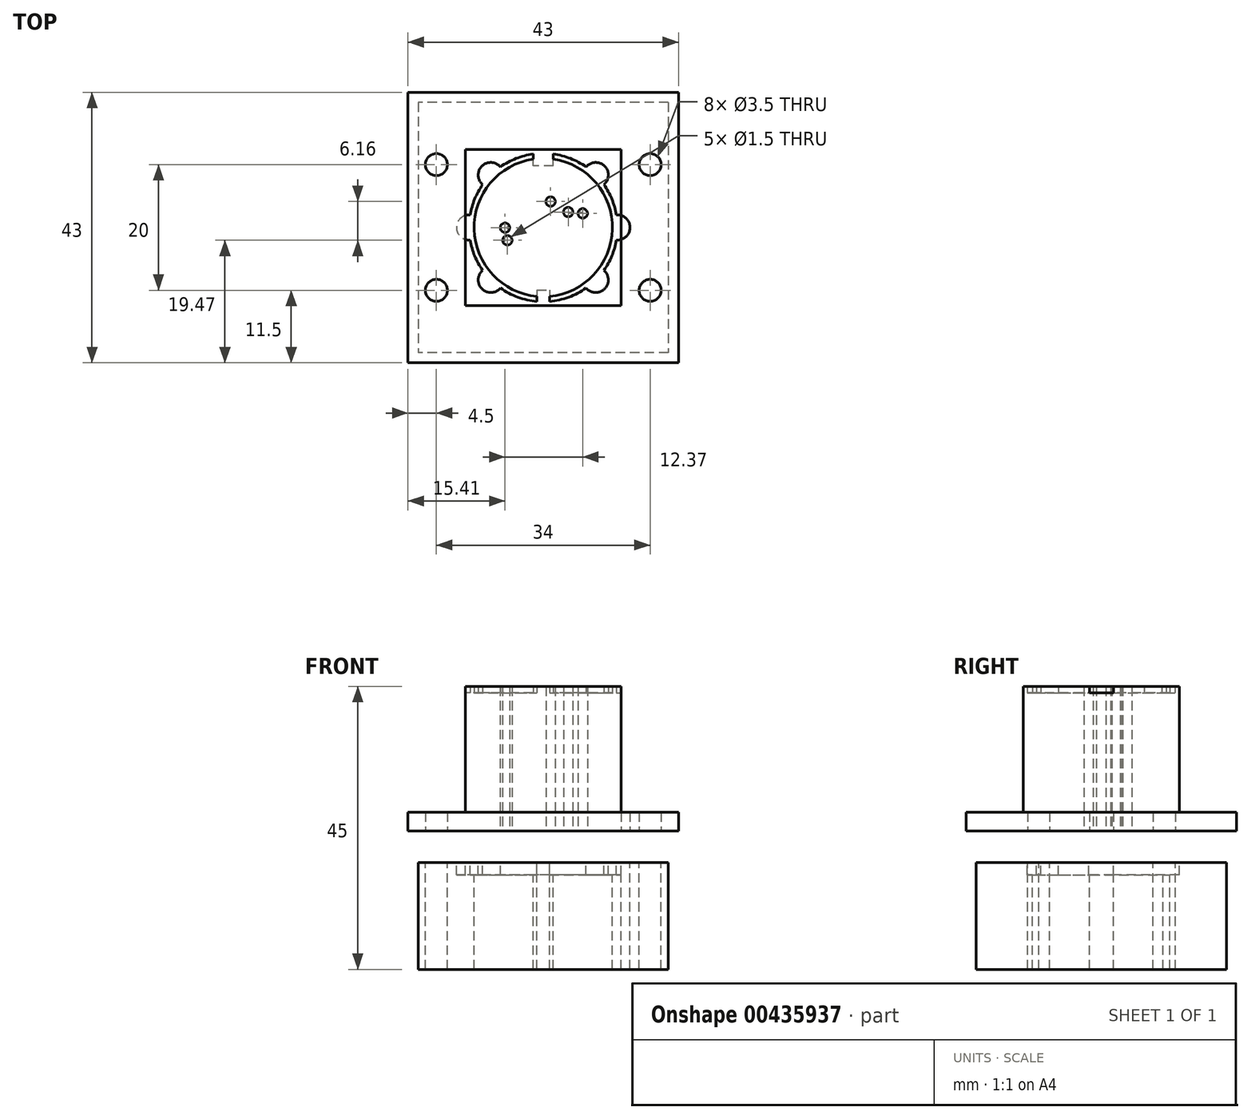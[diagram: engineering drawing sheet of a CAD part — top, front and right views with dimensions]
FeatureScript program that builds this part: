
annotation { "Feature Type Name" : "Feature", "Feature Type Description" : "" }
export const myFeature = defineFeature(function(context is Context, id is Id, definition is map)
    precondition{}
    {
        {
            var Q0;
            Q0=qCreatedBy(makeId("Top.planeOp"),FACE);
            var sketch = newSketch(context, id + "F0", { "sketchPlane" : qUnion([Q0])});
            skPoint(sketch, "E0", {"position": v(0, 0) * mm});
            skPoint(sketch, "E1", {"position": v(-6.1, -0.04) * mm});
            skPoint(sketch, "E2", {"position": v(-5.71, -2.03) * mm});
            skPoint(sketch, "E3", {"position": v(1.16, 4.13) * mm});
            skPoint(sketch, "E4", {"position": v(3.97, 2.45) * mm});
            skPoint(sketch, "E5", {"position": v(6.28, 2.24) * mm});
            skArc(sketch, "E6", {"start": v(-1.6, 11.7) * mm, "mid": v(-4.33, 10.98) * mm, "end": v(-6.81, 9.63) * mm});
            skPoint(sketch, "E7", {"position": v(0, 11.8) * mm});
            skPoint(sketch, "E8", {"position": v(0, -11.8) * mm});
            skPoint(sketch, "E9", {"position": v(11.8, 0) * mm});
            skPoint(sketch, "E10", {"position": v(-11.8, 0) * mm});
            skPoint(sketch, "E11", {"position": v(-8.34, 8.34) * mm});
            skPoint(sketch, "E12", {"position": v(8.34, 8.34) * mm});
            skLineSegment(sketch, "E13", {"start": v(-11.8, 0) * mm, "end": v(11.8, 0) * mm, "construction": true});
            skLineSegment(sketch, "E14", {"start": v(0, 11.8) * mm, "end": v(0, -11.8) * mm, "construction": true});
            skLineSegment(sketch, "E15", {"start": v(-8.34, 8.34) * mm, "end": v(0, 0) * mm, "construction": true});
            skLineSegment(sketch, "E16", {"start": v(8.34, 8.34) * mm, "end": v(0, 0) * mm, "construction": true});
            skLineSegment(sketch, "E17", {"start": v(8.34, -8.34) * mm, "end": v(0, 0) * mm, "construction": true});
            skLineSegment(sketch, "E18", {"start": v(-8.34, -8.34) * mm, "end": v(0, 0) * mm, "construction": true});
            skPoint(sketch, "E19", {"position": v(-8.34, -8.34) * mm});
            skPoint(sketch, "E20", {"position": v(8.34, -8.34) * mm});
            skLineSegment(sketch, "E21.bottom", {"start": v(1.6, 9.8) * mm, "end": v(-1.6, 9.8) * mm});
            skLineSegment(sketch, "E21.left", {"start": v(1.6, 9.8) * mm, "end": v(1.6, 11.7) * mm});
            skLineSegment(sketch, "E21.right", {"start": v(-1.6, 9.8) * mm, "end": v(-1.6, 11.7) * mm});
            skPoint(sketch, "E22", {"position": v(-1.6, 11.7) * mm});
            skPoint(sketch, "E23", {"position": v(1.6, 11.7) * mm});
            skLineSegment(sketch, "E24.bottom", {"start": v(-1, -9.97) * mm, "end": v(1, -9.97) * mm});
            skLineSegment(sketch, "E24.left", {"start": v(-1, -9.97) * mm, "end": v(-1, -11.76) * mm});
            skLineSegment(sketch, "E24.right", {"start": v(1, -9.97) * mm, "end": v(1, -11.76) * mm});
            skPoint(sketch, "E25", {"position": v(-1, -11.76) * mm});
            skPoint(sketch, "E26", {"position": v(1, -11.76) * mm});
            skArc(sketch, "E27.trimOffspring", {"start": v(1, -11.76) * mm, "mid": v(4.05, -11.08) * mm, "end": v(6.81, -9.63) * mm});
            skArc(sketch, "E28", {"start": v(-6.81, 9.63) * mm, "mid": v(-9.76, 9.76) * mm, "end": v(-9.63, 6.81) * mm});
            skArc(sketch, "E29", {"start": v(6.81, 9.63) * mm, "mid": v(9.76, 9.76) * mm, "end": v(9.63, 6.81) * mm});
            skArc(sketch, "E30", {"start": v(9.63, -6.81) * mm, "mid": v(9.76, -9.76) * mm, "end": v(6.81, -9.63) * mm});
            skArc(sketch, "E31", {"start": v(-9.63, -6.81) * mm, "mid": v(-9.76, -9.76) * mm, "end": v(-6.81, -9.63) * mm});
            skArc(sketch, "E32", {"start": v(-1.6, 10.88) * mm, "mid": v(-11, -0.3) * mm, "end": v(-1, -10.95) * mm});
            skCircle(sketch, "E33", {"center": v(6.28, 2.24) * mm, "radius": 0.75 * mm});
            skCircle(sketch, "E34", {"center": v(3.97, 2.45) * mm, "radius": 0.75 * mm});
            skCircle(sketch, "E35", {"center": v(1.16, 4.13) * mm, "radius": 0.75 * mm});
            skCircle(sketch, "E36", {"center": v(-6.1, -0.04) * mm, "radius": 0.75 * mm});
            skCircle(sketch, "E37", {"center": v(-5.71, -2.03) * mm, "radius": 0.75 * mm});
            skArc(sketch, "E38.trimOffspring", {"start": v(-9.63, 6.81) * mm, "mid": v(-10.9, 4.52) * mm, "end": v(-11.63, 2) * mm});
            skArc(sketch, "E39.trimOffspring", {"start": v(6.81, 9.63) * mm, "mid": v(4.33, 10.98) * mm, "end": v(1.6, 11.7) * mm});
            skArc(sketch, "E40.trimOffspring", {"start": v(-6.81, -9.63) * mm, "mid": v(-4.05, -11.08) * mm, "end": v(-1, -11.76) * mm});
            skArc(sketch, "E41.trimOffspring", {"start": v(9.63, -6.81) * mm, "mid": v(10.9, -4.52) * mm, "end": v(11.63, -2) * mm});
            skArc(sketch, "E42.trimOffspring", {"start": v(1, -10.95) * mm, "mid": v(11, -0.3) * mm, "end": v(1.6, 10.88) * mm});
            skPoint(sketch, "E43", {"position": v(1, -10.95) * mm});
            skArc(sketch, "E44", {"start": v(11.63, 2) * mm, "mid": v(13.8, 0) * mm, "end": v(11.63, -2) * mm});
            skArc(sketch, "E45", {"start": v(-11.63, 2) * mm, "mid": v(-13.8, 0) * mm, "end": v(-11.63, -2) * mm});
            skArc(sketch, "E46.trimOffspring", {"start": v(-11.63, -2) * mm, "mid": v(-10.9, -4.52) * mm, "end": v(-9.63, -6.81) * mm});
            skArc(sketch, "E47.trimOffspring", {"start": v(11.63, 2) * mm, "mid": v(10.9, 4.52) * mm, "end": v(9.63, 6.81) * mm});
            skLineSegment(sketch, "E48.bottom", {"start": v(20, 20) * mm, "end": v(-20, 20) * mm, "construction": true});
            skLineSegment(sketch, "E48.top", {"start": v(20, -20) * mm, "end": v(-20, -20) * mm, "construction": true});
            skLineSegment(sketch, "E48.left", {"start": v(20, 20) * mm, "end": v(20, -20) * mm, "construction": true});
            skLineSegment(sketch, "E48.right", {"start": v(-20, 20) * mm, "end": v(-20, -20) * mm, "construction": true});
            skLineSegment(sketch, "E49.bottom", {"start": v(12.5, 12.5) * mm, "end": v(-12.5, 12.5) * mm, "construction": true});
            skLineSegment(sketch, "E49.top", {"start": v(12.5, -12.5) * mm, "end": v(-12.5, -12.5) * mm, "construction": true});
            skLineSegment(sketch, "E49.left", {"start": v(12.5, 12.5) * mm, "end": v(12.5, -12.5) * mm, "construction": true});
            skLineSegment(sketch, "E49.right", {"start": v(-12.5, 12.5) * mm, "end": v(-12.5, -12.5) * mm, "construction": true});
            skPoint(sketch, "E50", {"position": v(-17, 10) * mm});
            skPoint(sketch, "E51", {"position": v(-17, -10) * mm});
            skPoint(sketch, "E52", {"position": v(17, 10) * mm});
            skPoint(sketch, "E53", {"position": v(17, -10) * mm});
            skCircle(sketch, "E54", {"center": v(-17, 10) * mm, "radius": 1.75 * mm});
            skCircle(sketch, "E55", {"center": v(-17, -10) * mm, "radius": 1.75 * mm});
            skCircle(sketch, "E56", {"center": v(17, -10) * mm, "radius": 1.75 * mm});
            skCircle(sketch, "E57", {"center": v(17, 10) * mm, "radius": 1.75 * mm});
            skLineSegment(sketch, "E58.bottom", {"start": v(21.5, -21.5) * mm, "end": v(-21.5, -21.5) * mm});
            skLineSegment(sketch, "E58.top", {"start": v(21.5, 21.5) * mm, "end": v(-21.5, 21.5) * mm});
            skLineSegment(sketch, "E58.left", {"start": v(21.5, -21.5) * mm, "end": v(21.5, 21.5) * mm});
            skLineSegment(sketch, "E58.right", {"start": v(-21.5, -21.5) * mm, "end": v(-21.5, 21.5) * mm});
            skLineSegment(sketch, "E59.0", {"start": v(12.4, 12.4) * mm, "end": v(-12.4, 12.4) * mm});
            skLineSegment(sketch, "E59.1", {"start": v(12.4, 12.4) * mm, "end": v(12.4, -12.4) * mm});
            skLineSegment(sketch, "E59.2", {"start": v(12.4, -12.4) * mm, "end": v(-12.4, -12.4) * mm});
            skLineSegment(sketch, "E59.3", {"start": v(-12.4, 12.4) * mm, "end": v(-12.4, -12.4) * mm});
            skLineSegment(sketch, "E60.0", {"start": v(19.9, 19.9) * mm, "end": v(-19.9, 19.9) * mm});
            skLineSegment(sketch, "E60.1", {"start": v(19.9, 19.9) * mm, "end": v(19.9, -19.9) * mm});
            skLineSegment(sketch, "E60.2", {"start": v(19.9, -19.9) * mm, "end": v(-19.9, -19.9) * mm});
            skLineSegment(sketch, "E60.3", {"start": v(-19.9, 19.9) * mm, "end": v(-19.9, -19.9) * mm});
            skSolve(sketch);
        }
        {
            var Q0;
            {var subQ9=sQuery(id+"F0.wireOp",EDGE,"E6");Q0=makeQuery(id+"F0.imprint","IMPRINT",FACE,{"disambiguationData":[TD([[makeQuery(id+"F0.imprint","IMPRINT",EDGE,{"derivedFrom":subQ9}),-1.0]])]});}
            var Q1;
            {var subQ5=sQuery(id+"F0.wireOp",EDGE,"E21.bottom");Q1=makeQuery(id+"F0.imprint","IMPRINT",FACE,{"disambiguationData":[TD([[makeQuery(id+"F0.imprint","IMPRINT",EDGE,{"derivedFrom":subQ5}),1.0]])]});}
            var Q2;
            {var subQ4=sQuery(id+"F0.wireOp",EDGE,"E6");Q2=makeQuery(id+"F0.imprint","IMPRINT",FACE,{"disambiguationData":[TD([[makeQuery(id+"F0.imprint","IMPRINT",EDGE,{"derivedFrom":subQ4}),1.0]])]});}
            var Q3;
            {var subQ0=sQuery(id+"F0.wireOp",EDGE,"E27.trimOffspring");Q3=makeQuery(id+"F0.imprint","IMPRINT",FACE,{"disambiguationData":[TD([[makeQuery(id+"F0.imprint","IMPRINT",EDGE,{"derivedFrom":subQ0}),1.0]])]});}
            var Q4;
            {var subQ7=sQuery(id+"F0.wireOp",EDGE,"E24.bottom");Q4=makeQuery(id+"F0.imprint","IMPRINT",FACE,{"disambiguationData":[TD([[makeQuery(id+"F0.imprint","IMPRINT",EDGE,{"derivedFrom":subQ7}),-1.0]])]});}
            var Q5;
            Q5=makeQuery(id+"F0.imprint","IMPRINT",FACE,{"disambiguationData":[TD([[makeQuery(id+"F0.imprint","IMPRINT",EDGE,{"derivedFrom":sQuery(id+"F0.wireOp",EDGE,"E54")}),-1.0]])]});
            var Q6;
            {var subQ0=sQuery(id+"F0.wireOp",EDGE,"E59.3");var subQ1=sQuery(id+"F0.wireOp",EDGE,"E45");var subQ2=makeQuery(id+"F0.imprint","INTERSECT",VERTEX,{"disambiguationData":[OD(0.0)],"derivedFrom":[subQ1,subQ0]});Q6=makeQuery(id+"F0.imprint","IMPRINT",FACE,{"disambiguationData":[TD([[makeQuery(id+"F0.imprint","IMPRINT",EDGE,{"disambiguationData":[TD([[subQ2,-1.0]])],"derivedFrom":subQ1}),1.0]])]});}
            var Q7;
            {var subQ0=sQuery(id+"F0.wireOp",EDGE,"E59.1");var subQ1=sQuery(id+"F0.wireOp",EDGE,"E44");var subQ2=makeQuery(id+"F0.imprint","INTERSECT",VERTEX,{"disambiguationData":[OD(0.0)],"derivedFrom":[subQ1,subQ0]});Q7=makeQuery(id+"F0.imprint","IMPRINT",FACE,{"disambiguationData":[TD([[makeQuery(id+"F0.imprint","IMPRINT",EDGE,{"disambiguationData":[TD([[subQ2,-1.0]])],"derivedFrom":subQ1}),-1.0]])]});}
            var Q8;
            Q8=makeQuery(id+"F0.imprint","IMPRINT",FACE,{"disambiguationData":[TD([[makeQuery(id+"F0.imprint","IMPRINT",EDGE,{"derivedFrom":sQuery(id+"F0.wireOp",EDGE,"E58.bottom")}),-1.0]])]});
            extrude(context, id + "F1", {"entities" : qUnion([Q0, Q1, Q2, Q3, Q4, Q5, Q6, Q7, Q8]), "depth" : 8 * mm, "hasSecondDirection" : true, "secondDirectionOppositeDirection" : false, "secondDirectionDepth" : 5 * mm});
        }
        {
            var Q0;
            {var subQ1=sQuery(id+"F0.wireOp",EDGE,"E6");Q0=makeQuery(id+"F0.imprint","IMPRINT",FACE,{"disambiguationData":[TD([[makeQuery(id+"F0.imprint","IMPRINT",EDGE,{"derivedFrom":subQ1}),-1.0]])]});}
            var Q1;
            {var subQ5=sQuery(id+"F0.wireOp",EDGE,"E21.bottom");Q1=makeQuery(id+"F0.imprint","IMPRINT",FACE,{"disambiguationData":[TD([[makeQuery(id+"F0.imprint","IMPRINT",EDGE,{"derivedFrom":subQ5}),1.0]])]});}
            var Q2;
            {var subQ6=sQuery(id+"F0.wireOp",EDGE,"E6");Q2=makeQuery(id+"F0.imprint","IMPRINT",FACE,{"disambiguationData":[TD([[makeQuery(id+"F0.imprint","IMPRINT",EDGE,{"derivedFrom":subQ6}),1.0]])]});}
            var Q3;
            {var subQ7=sQuery(id+"F0.wireOp",EDGE,"E24.bottom");Q3=makeQuery(id+"F0.imprint","IMPRINT",FACE,{"disambiguationData":[TD([[makeQuery(id+"F0.imprint","IMPRINT",EDGE,{"derivedFrom":subQ7}),-1.0]])]});}
            var Q4;
            {var subQ9=sQuery(id+"F0.wireOp",EDGE,"E27.trimOffspring");Q4=makeQuery(id+"F0.imprint","IMPRINT",FACE,{"disambiguationData":[TD([[makeQuery(id+"F0.imprint","IMPRINT",EDGE,{"derivedFrom":subQ9}),1.0]])]});}
            extrude(context, id + "F2", {"entities" : qUnion([Q0, Q1, Q2, Q3, Q4]), "operationType" : NewBodyOperationType.ADD, "depth" : 28 * mm, "hasSecondDirection" : true, "secondDirectionOppositeDirection" : false, "secondDirectionDepth" : 8 * mm});
        }
        {
            var Q0;
            {var subQ6=sQuery(id+"F0.wireOp",EDGE,"E6");Q0=makeQuery(id+"F0.imprint","IMPRINT",FACE,{"disambiguationData":[TD([[makeQuery(id+"F0.imprint","IMPRINT",EDGE,{"derivedFrom":subQ6}),1.0]])]});}
            var Q1;
            {var subQ9=sQuery(id+"F0.wireOp",EDGE,"E27.trimOffspring");Q1=makeQuery(id+"F0.imprint","IMPRINT",FACE,{"disambiguationData":[TD([[makeQuery(id+"F0.imprint","IMPRINT",EDGE,{"derivedFrom":subQ9}),1.0]])]});}
            extrude(context, id + "F3", {"entities" : qUnion([Q0, Q1]), "operationType" : NewBodyOperationType.REMOVE, "depth" : 28 * mm, "hasSecondDirection" : true, "secondDirectionOppositeDirection" : false, "secondDirectionDepth" : 27 * mm});
        }
        {
            var Q0;
            Q0=makeQuery(id+"F0.imprint","IMPRINT",FACE,{"disambiguationData":[TD([[makeQuery(id+"F0.imprint","IMPRINT",EDGE,{"derivedFrom":sQuery(id+"F0.wireOp",EDGE,"E54")}),-1.0]])]});
            var Q1;
            {var subQ1=sQuery(id+"F0.wireOp",EDGE,"E6");Q1=makeQuery(id+"F0.imprint","IMPRINT",FACE,{"disambiguationData":[TD([[makeQuery(id+"F0.imprint","IMPRINT",EDGE,{"derivedFrom":subQ1}),-1.0]])]});}
            var Q2;
            {var subQ7=sQuery(id+"F0.wireOp",EDGE,"E24.bottom");Q2=makeQuery(id+"F0.imprint","IMPRINT",FACE,{"disambiguationData":[TD([[makeQuery(id+"F0.imprint","IMPRINT",EDGE,{"derivedFrom":subQ7}),-1.0]])]});}
            var Q3;
            {var subQ5=sQuery(id+"F0.wireOp",EDGE,"E21.bottom");Q3=makeQuery(id+"F0.imprint","IMPRINT",FACE,{"disambiguationData":[TD([[makeQuery(id+"F0.imprint","IMPRINT",EDGE,{"derivedFrom":subQ5}),1.0]])]});}
            var Q4;
            {var subQ6=sQuery(id+"F0.wireOp",EDGE,"E6");Q4=makeQuery(id+"F0.imprint","IMPRINT",FACE,{"disambiguationData":[TD([[makeQuery(id+"F0.imprint","IMPRINT",EDGE,{"derivedFrom":subQ6}),1.0]])]});}
            var Q5;
            {var subQ9=sQuery(id+"F0.wireOp",EDGE,"E27.trimOffspring");Q5=makeQuery(id+"F0.imprint","IMPRINT",FACE,{"disambiguationData":[TD([[makeQuery(id+"F0.imprint","IMPRINT",EDGE,{"derivedFrom":subQ9}),1.0]])]});}
            var Q6;
            {var subQ0=sQuery(id+"F0.wireOp",EDGE,"E59.3");var subQ1=sQuery(id+"F0.wireOp",EDGE,"E45");var subQ2=makeQuery(id+"F0.imprint","INTERSECT",VERTEX,{"disambiguationData":[OD(0.0)],"derivedFrom":[subQ1,subQ0]});Q6=makeQuery(id+"F0.imprint","IMPRINT",FACE,{"disambiguationData":[TD([[makeQuery(id+"F0.imprint","IMPRINT",EDGE,{"disambiguationData":[TD([[subQ2,-1.0]])],"derivedFrom":subQ1}),1.0]])]});}
            var Q7;
            {var subQ0=sQuery(id+"F0.wireOp",EDGE,"E59.1");var subQ1=sQuery(id+"F0.wireOp",EDGE,"E44");var subQ2=makeQuery(id+"F0.imprint","INTERSECT",VERTEX,{"disambiguationData":[OD(0.0)],"derivedFrom":[subQ1,subQ0]});Q7=makeQuery(id+"F0.imprint","IMPRINT",FACE,{"disambiguationData":[TD([[makeQuery(id+"F0.imprint","IMPRINT",EDGE,{"disambiguationData":[TD([[subQ2,-1.0]])],"derivedFrom":subQ1}),-1.0]])]});}
            var Q8;
            Q8=makeQuery(id+"F0.imprint","IMPRINT",FACE,{"disambiguationData":[TD([[makeQuery(id+"F0.imprint","IMPRINT",EDGE,{"derivedFrom":sQuery(id+"F0.wireOp",EDGE,"E33")}),1.0]])]});
            var Q9;
            Q9=makeQuery(id+"F0.imprint","IMPRINT",FACE,{"disambiguationData":[TD([[makeQuery(id+"F0.imprint","IMPRINT",EDGE,{"derivedFrom":sQuery(id+"F0.wireOp",EDGE,"E34")}),1.0]])]});
            var Q10;
            Q10=makeQuery(id+"F0.imprint","IMPRINT",FACE,{"disambiguationData":[TD([[makeQuery(id+"F0.imprint","IMPRINT",EDGE,{"derivedFrom":sQuery(id+"F0.wireOp",EDGE,"E35")}),1.0]])]});
            var Q11;
            Q11=makeQuery(id+"F0.imprint","IMPRINT",FACE,{"disambiguationData":[TD([[makeQuery(id+"F0.imprint","IMPRINT",EDGE,{"derivedFrom":sQuery(id+"F0.wireOp",EDGE,"E36")}),1.0]])]});
            var Q12;
            Q12=makeQuery(id+"F0.imprint","IMPRINT",FACE,{"disambiguationData":[TD([[makeQuery(id+"F0.imprint","IMPRINT",EDGE,{"derivedFrom":sQuery(id+"F0.wireOp",EDGE,"E37")}),1.0]])]});
            extrude(context, id + "F4", {"entities" : qUnion([Q0, Q1, Q2, Q3, Q4, Q5, Q6, Q7, Q8, Q9, Q10, Q11, Q12]), "oppositeDirection" : true, "depth" : 17 * mm});
        }
        {
            var Q0;
            {var subQ6=sQuery(id+"F0.wireOp",EDGE,"E6");Q0=makeQuery(id+"F0.imprint","IMPRINT",FACE,{"disambiguationData":[TD([[makeQuery(id+"F0.imprint","IMPRINT",EDGE,{"derivedFrom":subQ6}),1.0]])]});}
            var Q1;
            {var subQ5=sQuery(id+"F0.wireOp",EDGE,"E21.bottom");Q1=makeQuery(id+"F0.imprint","IMPRINT",FACE,{"disambiguationData":[TD([[makeQuery(id+"F0.imprint","IMPRINT",EDGE,{"derivedFrom":subQ5}),1.0]])]});}
            var Q2;
            {var subQ0=sQuery(id+"F0.wireOp",EDGE,"E59.3");var subQ1=sQuery(id+"F0.wireOp",EDGE,"E45");var subQ2=makeQuery(id+"F0.imprint","INTERSECT",VERTEX,{"disambiguationData":[OD(0.0)],"derivedFrom":[subQ1,subQ0]});Q2=makeQuery(id+"F0.imprint","IMPRINT",FACE,{"disambiguationData":[TD([[makeQuery(id+"F0.imprint","IMPRINT",EDGE,{"disambiguationData":[TD([[subQ2,-1.0]])],"derivedFrom":subQ1}),1.0]])]});}
            var Q3;
            {var subQ9=sQuery(id+"F0.wireOp",EDGE,"E27.trimOffspring");Q3=makeQuery(id+"F0.imprint","IMPRINT",FACE,{"disambiguationData":[TD([[makeQuery(id+"F0.imprint","IMPRINT",EDGE,{"derivedFrom":subQ9}),1.0]])]});}
            var Q4;
            {var subQ0=sQuery(id+"F0.wireOp",EDGE,"E59.1");var subQ1=sQuery(id+"F0.wireOp",EDGE,"E44");var subQ2=makeQuery(id+"F0.imprint","INTERSECT",VERTEX,{"disambiguationData":[OD(0.0)],"derivedFrom":[subQ1,subQ0]});Q4=makeQuery(id+"F0.imprint","IMPRINT",FACE,{"disambiguationData":[TD([[makeQuery(id+"F0.imprint","IMPRINT",EDGE,{"disambiguationData":[TD([[subQ2,-1.0]])],"derivedFrom":subQ1}),-1.0]])]});}
            var Q5;
            Q5=makeQuery(id+"F0.imprint","IMPRINT",FACE,{"disambiguationData":[TD([[makeQuery(id+"F0.imprint","IMPRINT",EDGE,{"derivedFrom":sQuery(id+"F0.wireOp",EDGE,"E37")}),1.0]])]});
            var Q6;
            Q6=makeQuery(id+"F0.imprint","IMPRINT",FACE,{"disambiguationData":[TD([[makeQuery(id+"F0.imprint","IMPRINT",EDGE,{"derivedFrom":sQuery(id+"F0.wireOp",EDGE,"E36")}),1.0]])]});
            var Q7;
            Q7=makeQuery(id+"F0.imprint","IMPRINT",FACE,{"disambiguationData":[TD([[makeQuery(id+"F0.imprint","IMPRINT",EDGE,{"derivedFrom":sQuery(id+"F0.wireOp",EDGE,"E35")}),1.0]])]});
            var Q8;
            Q8=makeQuery(id+"F0.imprint","IMPRINT",FACE,{"disambiguationData":[TD([[makeQuery(id+"F0.imprint","IMPRINT",EDGE,{"derivedFrom":sQuery(id+"F0.wireOp",EDGE,"E34")}),1.0]])]});
            var Q9;
            Q9=makeQuery(id+"F0.imprint","IMPRINT",FACE,{"disambiguationData":[TD([[makeQuery(id+"F0.imprint","IMPRINT",EDGE,{"derivedFrom":sQuery(id+"F0.wireOp",EDGE,"E33")}),1.0]])]});
            extrude(context, id + "F5", {"entities" : qUnion([Q0, Q1, Q2, Q3, Q4, Q5, Q6, Q7, Q8, Q9]), "operationType" : NewBodyOperationType.REMOVE, "oppositeDirection" : true, "depth" : 2 * mm});
        }
        {
            var Q0;
            {var subQ5=sQuery(id+"F0.wireOp",EDGE,"E21.bottom");Q0=makeQuery(id+"F0.imprint","IMPRINT",FACE,{"disambiguationData":[TD([[makeQuery(id+"F0.imprint","IMPRINT",EDGE,{"derivedFrom":subQ5}),1.0]])]});}
            var Q1;
            Q1=makeQuery(id+"F0.imprint","IMPRINT",FACE,{"disambiguationData":[TD([[makeQuery(id+"F0.imprint","IMPRINT",EDGE,{"derivedFrom":sQuery(id+"F0.wireOp",EDGE,"E36")}),1.0]])]});
            var Q2;
            Q2=makeQuery(id+"F0.imprint","IMPRINT",FACE,{"disambiguationData":[TD([[makeQuery(id+"F0.imprint","IMPRINT",EDGE,{"derivedFrom":sQuery(id+"F0.wireOp",EDGE,"E37")}),1.0]])]});
            var Q3;
            Q3=makeQuery(id+"F0.imprint","IMPRINT",FACE,{"disambiguationData":[TD([[makeQuery(id+"F0.imprint","IMPRINT",EDGE,{"derivedFrom":sQuery(id+"F0.wireOp",EDGE,"E35")}),1.0]])]});
            var Q4;
            Q4=makeQuery(id+"F0.imprint","IMPRINT",FACE,{"disambiguationData":[TD([[makeQuery(id+"F0.imprint","IMPRINT",EDGE,{"derivedFrom":sQuery(id+"F0.wireOp",EDGE,"E34")}),1.0]])]});
            var Q5;
            Q5=makeQuery(id+"F0.imprint","IMPRINT",FACE,{"disambiguationData":[TD([[makeQuery(id+"F0.imprint","IMPRINT",EDGE,{"derivedFrom":sQuery(id+"F0.wireOp",EDGE,"E33")}),1.0]])]});
            extrude(context, id + "F6", {"entities" : qUnion([Q0, Q1, Q2, Q3, Q4, Q5]), "operationType" : NewBodyOperationType.REMOVE, "oppositeDirection" : true, "depth" : 22 * mm});
        }
    });
